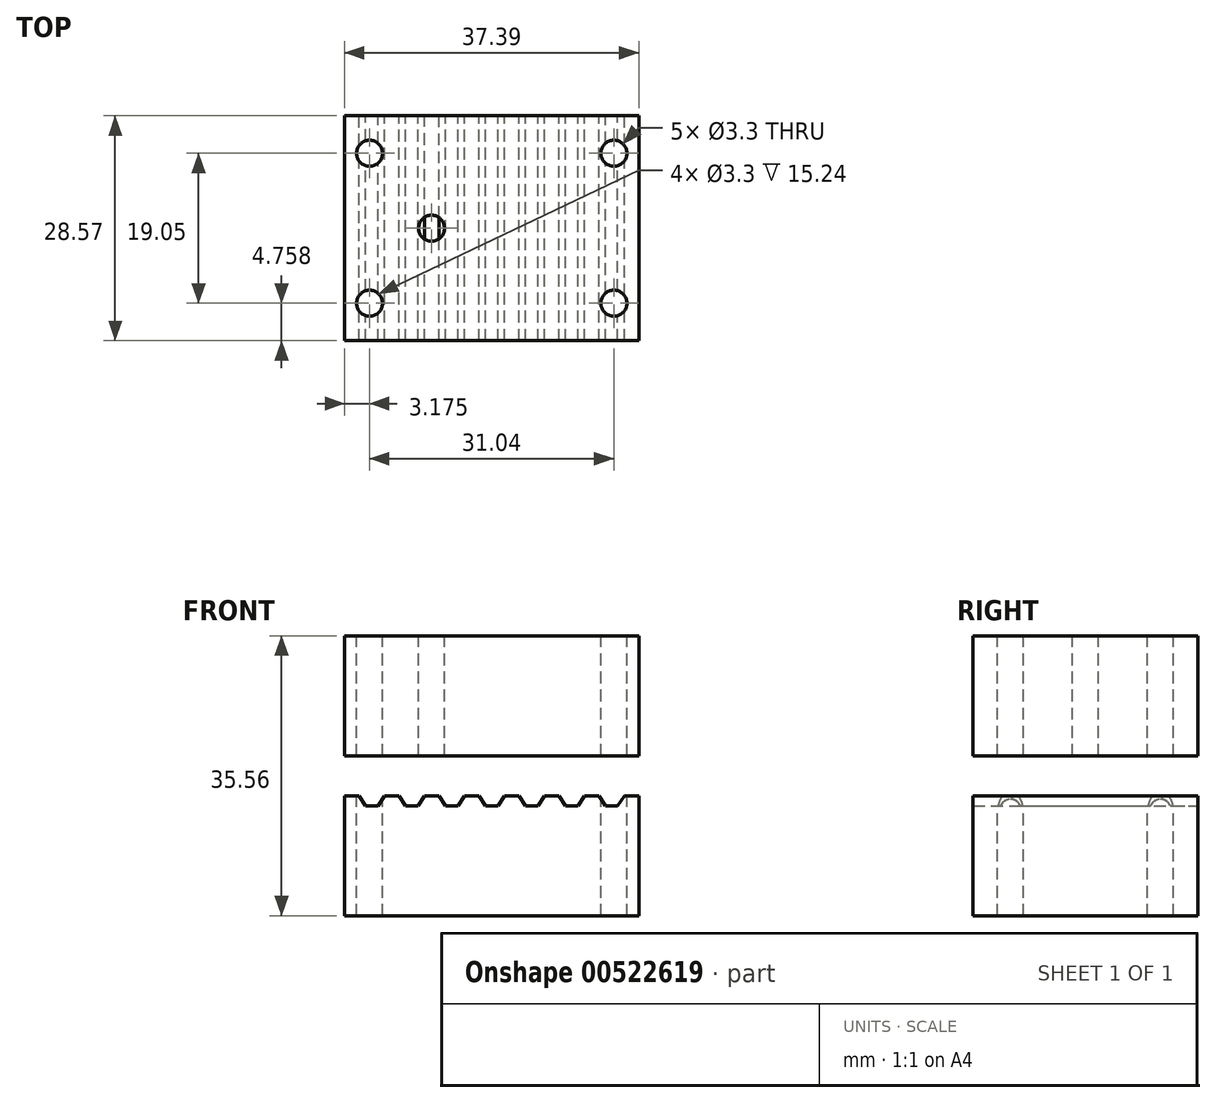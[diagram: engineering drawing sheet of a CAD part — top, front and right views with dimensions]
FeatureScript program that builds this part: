
annotation { "Feature Type Name" : "Feature", "Feature Type Description" : "" }
export const myFeature = defineFeature(function(context is Context, id is Id, definition is map)
    precondition{}
    {
        {
            var Q0;
            Q0=qCreatedBy(makeId("Front.planeOp"),FACE);
            var sketch = newSketch(context, id + "F0", { "sketchPlane" : qUnion([Q0])});
            skLineSegment(sketch, "E0", {"start": v(1.85, 0) * mm, "end": v(2.69, -1.27) * mm});
            skLineSegment(sketch, "E1", {"start": v(2.69, -1.27) * mm, "end": v(4.24, -1.27) * mm});
            skLineSegment(sketch, "E2", {"start": v(4.24, -1.27) * mm, "end": v(5.08, 0) * mm});
            skLineSegment(sketch, "E3", {"start": v(5.08, 0) * mm, "end": v(6.93, 0) * mm});
            skLineSegment(sketch, "E4", {"start": v(6.93, 0) * mm, "end": v(7.77, -1.27) * mm});
            skLineSegment(sketch, "E5", {"start": v(7.77, -1.27) * mm, "end": v(9.32, -1.27) * mm});
            skLineSegment(sketch, "E6", {"start": v(9.32, -1.27) * mm, "end": v(10.16, 0) * mm});
            skPoint(sketch, "E7", {"position": v(3.47, -1.27) * mm});
            skPoint(sketch, "E8", {"position": v(8.55, -1.27) * mm});
            skLineSegment(sketch, "E9", {"start": v(1.85, 0) * mm, "end": v(0, 0) * mm});
            skLineSegment(sketch, "E10", {"start": v(0, 0) * mm, "end": v(0, -15.24) * mm});
            skLineSegment(sketch, "E11", {"start": v(0, -15.24) * mm, "end": v(37.39, -15.24) * mm});
            skLineSegment(sketch, "E12", {"start": v(37.39, -15.24) * mm, "end": v(37.39, 0) * mm});
            skPoint(sketch, "E13", {"position": v(0.93, 0) * mm});
            skPoint(sketch, "E14", {"position": v(6, 0) * mm});
            skLineSegment(sketch, "E15", {"start": v(12.01, 0) * mm, "end": v(12.85, -1.27) * mm});
            skLineSegment(sketch, "E16", {"start": v(12.85, -1.27) * mm, "end": v(14.4, -1.27) * mm});
            skLineSegment(sketch, "E17", {"start": v(14.4, -1.27) * mm, "end": v(15.24, 0) * mm});
            skLineSegment(sketch, "E18", {"start": v(15.24, 0) * mm, "end": v(17.1, 0) * mm});
            skLineSegment(sketch, "E19", {"start": v(17.1, 0) * mm, "end": v(17.93, -1.27) * mm});
            skLineSegment(sketch, "E20", {"start": v(17.93, -1.27) * mm, "end": v(19.48, -1.27) * mm});
            skLineSegment(sketch, "E21", {"start": v(19.48, -1.27) * mm, "end": v(20.32, 0) * mm});
            skPoint(sketch, "E22", {"position": v(13.63, -1.27) * mm});
            skPoint(sketch, "E23", {"position": v(18.7, -1.27) * mm});
            skLineSegment(sketch, "E24", {"start": v(12.01, 0) * mm, "end": v(10.16, 0) * mm});
            skPoint(sketch, "E25", {"position": v(11.09, 0) * mm});
            skPoint(sketch, "E26", {"position": v(16.17, 0) * mm});
            skLineSegment(sketch, "E27", {"start": v(22.17, 0) * mm, "end": v(23, -1.27) * mm});
            skLineSegment(sketch, "E28", {"start": v(23, -1.27) * mm, "end": v(24.56, -1.27) * mm});
            skLineSegment(sketch, "E29", {"start": v(24.56, -1.27) * mm, "end": v(25.4, 0) * mm});
            skLineSegment(sketch, "E30", {"start": v(25.4, 0) * mm, "end": v(27.25, 0) * mm});
            skLineSegment(sketch, "E31", {"start": v(27.25, 0) * mm, "end": v(28.09, -1.27) * mm});
            skLineSegment(sketch, "E32", {"start": v(28.09, -1.27) * mm, "end": v(29.64, -1.27) * mm});
            skLineSegment(sketch, "E33", {"start": v(29.64, -1.27) * mm, "end": v(30.48, 0) * mm});
            skPoint(sketch, "E34", {"position": v(23.79, -1.27) * mm});
            skPoint(sketch, "E35", {"position": v(28.87, -1.27) * mm});
            skLineSegment(sketch, "E36", {"start": v(22.17, 0) * mm, "end": v(20.32, 0) * mm});
            skPoint(sketch, "E37", {"position": v(21.25, 0) * mm});
            skPoint(sketch, "E38", {"position": v(26.33, 0) * mm});
            skLineSegment(sketch, "E39", {"start": v(30.48, 0) * mm, "end": v(32.33, 0) * mm});
            skLineSegment(sketch, "E40", {"start": v(32.33, 0) * mm, "end": v(33.17, -1.27) * mm});
            skLineSegment(sketch, "E41", {"start": v(33.17, -1.27) * mm, "end": v(34.7, -1.27) * mm});
            skLineSegment(sketch, "E42", {"start": v(34.7, -1.27) * mm, "end": v(35.54, 0) * mm});
            skPoint(sketch, "E43", {"position": v(33.93, -1.27) * mm});
            skPoint(sketch, "E44", {"position": v(31.4, 0) * mm});
            skLineSegment(sketch, "E45", {"start": v(35.54, 0) * mm, "end": v(37.39, 0) * mm});
            skLineSegment(sketch, "E46.bottom", {"start": v(0, 5.08) * mm, "end": v(37.39, 5.08) * mm});
            skLineSegment(sketch, "E46.top", {"start": v(0, 20.32) * mm, "end": v(37.39, 20.32) * mm});
            skLineSegment(sketch, "E46.left", {"start": v(0, 5.08) * mm, "end": v(0, 20.32) * mm});
            skLineSegment(sketch, "E46.right", {"start": v(37.39, 5.08) * mm, "end": v(37.39, 20.32) * mm});
            skSolve(sketch);
        }
        {
            var Q0;
            Q0=makeQuery(id+"F0.imprint","IMPRINT",FACE,{"disambiguationData":[TD([[makeQuery(id+"F0.imprint","IMPRINT",EDGE,{"derivedFrom":sQuery(id+"F0.wireOp",EDGE,"E46.bottom")}),1.0]])]});
            var Q1;
            Q1=makeQuery(id+"F0.imprint","IMPRINT",FACE,{"disambiguationData":[TD([[makeQuery(id+"F0.imprint","IMPRINT",EDGE,{"derivedFrom":sQuery(id+"F0.wireOp",EDGE,"E0")}),-1.0]])]});
            extrude(context, id + "F1", {"entities" : qUnion([Q0, Q1]), "depth" : 28.57 * mm, "offsetDistance" : 25.4 * mm});
        }
        {
            var Q0;
            Q0=makeQuery(id+"F1.opExtrude","SWEPT_FACE",FACE,{"disambiguationData":[OSD([sQuery(id+"F0.wireOp",EDGE,"E46.top")])]});
            var sketch = newSketch(context, id + "F2", { "sketchPlane" : qUnion([Q0])});
            skPoint(sketch, "E47", {"position": v(0, -9.53) * mm});
            skPoint(sketch, "E48", {"position": v(0, -19.05) * mm});
            skPoint(sketch, "E49", {"position": v(0, -23.81) * mm});
            skLineSegment(sketch, "E50", {"start": v(0, -23.81) * mm, "end": v(37.39, -23.81) * mm, "construction": true});
            skCircle(sketch, "E51", {"center": v(3.18, -23.81) * mm, "radius": 1.65 * mm});
            skCircle(sketch, "E52", {"center": v(34.21, -23.81) * mm, "radius": 1.65 * mm});
            skCircle(sketch, "E53", {"center": v(3.18, -4.76) * mm, "radius": 1.65 * mm});
            skCircle(sketch, "E54", {"center": v(34.21, -4.76) * mm, "radius": 1.65 * mm});
            skPoint(sketch, "E55", {"position": v(0, -4.76) * mm});
            skLineSegment(sketch, "E56", {"start": v(0, -4.76) * mm, "end": v(37.39, -4.76) * mm, "construction": true});
            skSolve(sketch);
        }
        {
            var Q0;
            Q0=makeQuery(id+"F2.imprint","IMPRINT",FACE,{"disambiguationData":[TD([[makeQuery(id+"F2.imprint","IMPRINT",EDGE,{"derivedFrom":sQuery(id+"F2.wireOp",EDGE,"E53")}),1.0]])]});
            var Q1;
            Q1=makeQuery(id+"F2.imprint","IMPRINT",FACE,{"disambiguationData":[TD([[makeQuery(id+"F2.imprint","IMPRINT",EDGE,{"derivedFrom":sQuery(id+"F2.wireOp",EDGE,"E51")}),1.0]])]});
            var Q2;
            Q2=makeQuery(id+"F2.imprint","IMPRINT",FACE,{"disambiguationData":[TD([[makeQuery(id+"F2.imprint","IMPRINT",EDGE,{"derivedFrom":sQuery(id+"F2.wireOp",EDGE,"E54")}),1.0]])]});
            var Q3;
            Q3=makeQuery(id+"F2.imprint","IMPRINT",FACE,{"disambiguationData":[TD([[makeQuery(id+"F2.imprint","IMPRINT",EDGE,{"derivedFrom":sQuery(id+"F2.wireOp",EDGE,"E52")}),1.0]])]});
            extrude(context, id + "F3", {"entities" : qUnion([Q0, Q1, Q2, Q3]), "operationType" : NewBodyOperationType.REMOVE, "endBound" : BoundingType.THROUGH_ALL, "oppositeDirection" : true, "depth" : 25.4 * mm, "offsetDistance" : 25.4 * mm});
        }
        {
            var Q0;
            Q0=makeQuery(id+"F1.opExtrude","SWEPT_FACE",FACE,{"disambiguationData":[OSD([sQuery(id+"F0.wireOp",EDGE,"E46.top")])]});
            var sketch = newSketch(context, id + "F4", { "sketchPlane" : qUnion([Q0])});
            skLineSegment(sketch, "E57", {"start": v(11.05, 0) * mm, "end": v(11.05, -28.58) * mm, "construction": true});
            skLineSegment(sketch, "E58", {"start": v(0, -14.29) * mm, "end": v(11.05, -14.29) * mm, "construction": true});
            skCircle(sketch, "E59", {"center": v(11.05, -14.29) * mm, "radius": 1.65 * mm});
            skSolve(sketch);
        }
        {
            var Q0;
            Q0=makeQuery(id+"F4.imprint","IMPRINT",FACE,{"disambiguationData":[TD([[makeQuery(id+"F4.imprint","IMPRINT",EDGE,{"derivedFrom":sQuery(id+"F4.wireOp",EDGE,"E59")}),1.0]])]});
            var Q1;
            Q1=makeQuery(id+"F1.opExtrude","SWEPT_FACE",FACE,{"disambiguationData":[OSD([sQuery(id+"F0.wireOp",EDGE,"E46.bottom")])]});
            extrude(context, id + "F5", {"entities" : qUnion([Q0]), "operationType" : NewBodyOperationType.REMOVE, "endBound" : BoundingType.UP_TO_SURFACE, "oppositeDirection" : true, "depth" : 25.4 * mm, "endBoundEntityFace" : qUnion([Q1]), "offsetDistance" : 25.4 * mm});
        }
    });
